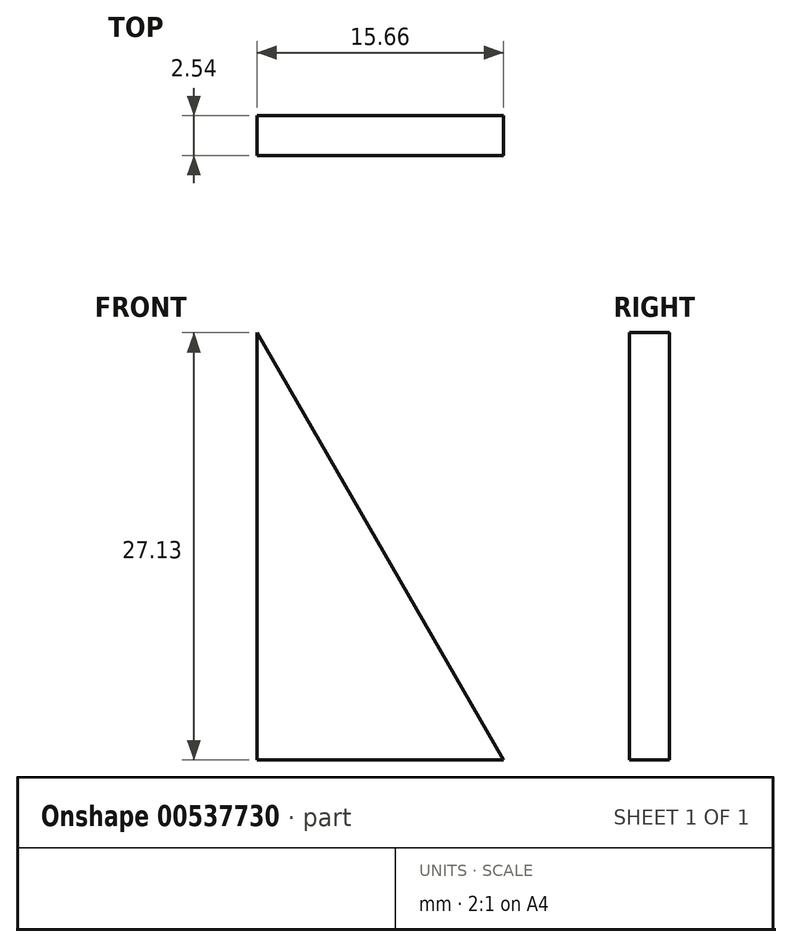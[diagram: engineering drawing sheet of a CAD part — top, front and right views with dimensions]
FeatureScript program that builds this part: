
annotation { "Feature Type Name" : "Feature", "Feature Type Description" : "" }
export const myFeature = defineFeature(function(context is Context, id is Id, definition is map)
    precondition{}
    {
        {
            var Q0;
            Q0=qCreatedBy(makeId("Front.planeOp"),FACE);
            var sketch = newSketch(context, id + "F0", { "sketchPlane" : qUnion([Q0])});
            skLineSegment(sketch, "E0", {"start": v(0, 0) * mm, "end": v(0, 27.13) * mm});
            skLineSegment(sketch, "E1", {"start": v(0, 27.13) * mm, "end": v(15.66, 0) * mm});
            skLineSegment(sketch, "E2", {"start": v(15.66, 0) * mm, "end": v(0, 0) * mm});
            skSolve(sketch);
        }
        {
            var Q0;
            Q0=makeQuery(id+"F0.imprint","IMPRINT",FACE,{"disambiguationData":[TD([[makeQuery(id+"F0.imprint","IMPRINT",EDGE,{"derivedFrom":sQuery(id+"F0.wireOp",EDGE,"E0")}),-1.0]])]});
            extrude(context, id + "F1", {"entities" : qUnion([Q0]), "depth" : 2.54 * mm, "offsetDistance" : 25.4 * mm});
        }
    });
